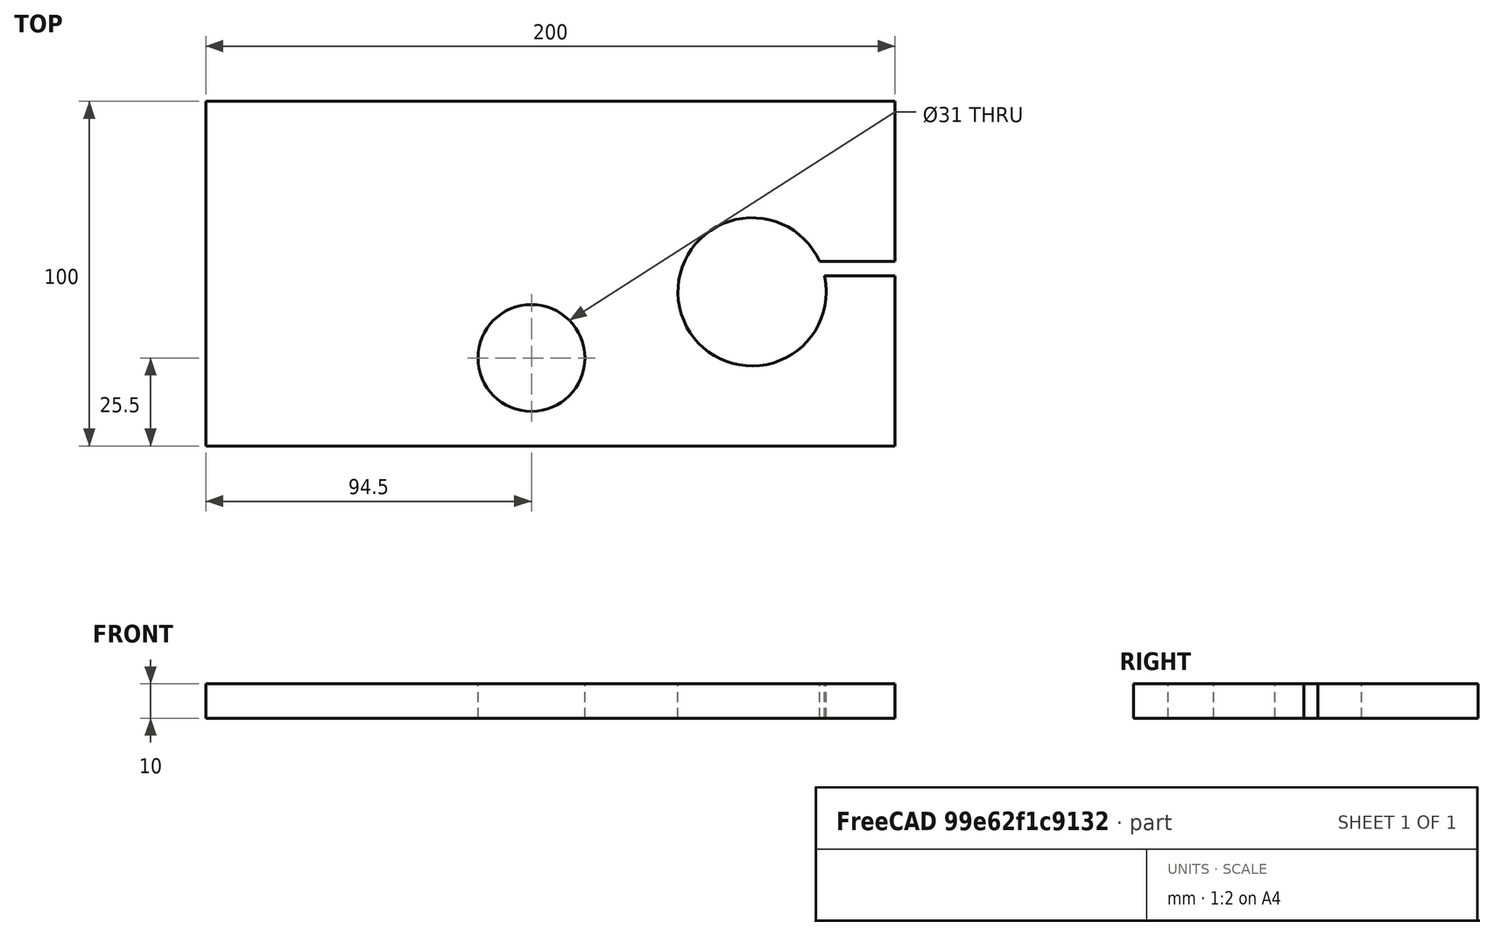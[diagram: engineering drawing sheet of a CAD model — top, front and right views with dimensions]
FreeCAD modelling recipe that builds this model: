
FCSTD DOCUMENT  (FreeCAD 0.16R6449 (Git))
Label: dust_collector_plate
License: All rights reserved
LicenseURL: http://en.wikipedia.org/wiki/All_rights_reserved
objects: Part::Cut×4, Part::Box×3, Part::Cylinder×3, Part::Fuse×1
note: 11 computed .brp shape members not serialized (recipe doc carries the construction recipe); baked Part::Feature solids carry a one-line shape summary decoded from their .brp

FEATURE [Part::Box] Box  label="spindle holder plate"
  Height = 10
  Length = 80
  Width = 80
FEATURE [Part::Cylinder] Cylinder
  Angle = 360
  Height = 10
  Placement = pos=(38.5,44.7,0) rot=(0,0,1;0rad)
  Radius = 21.5
FEATURE [Part::Box] Box001  label="dust collector plate"
  Height = 10
  Length = 200
  Placement = pos=(-120,0,0) rot=(0,0,1;0rad)
  Width = 100
FEATURE [Part::Cylinder] Cylinder001
  Angle = 360
  Height = 10
  Placement = pos=(38.5,44.7,0) rot=(0,0,1;0rad)
  Radius = 21.5
FEATURE [Part::Cut] Cut
  Base = -> Box
  Tool = -> Cylinder
FEATURE [Part::Cut] Cut001
  Base = -> Box001
  Tool = -> Cylinder001
FEATURE [Part::Fuse] Fusion
  Base = -> Cut
  Tool = -> Cut001
FEATURE [Part::Cylinder] Cylinder002
  Angle = 360
  Height = 10
  Placement = pos=(-25.5,25.5,0) rot=(0,0,1;0rad)
  Radius = 15.5
FEATURE [Part::Cut] Cut002
  Base = -> Fusion
  Tool = -> Cylinder002
FEATURE [Part::Box] Box002  label="Cube"
  Height = 10
  Length = 22
  Placement = pos=(58,49.36,0) rot=(0,0,1;0rad)
  Width = 4.15
  expr: Placement.Base.x = 58
FEATURE [Part::Cut] Cut003
  Base = -> Cut002
  Tool = -> Box002
